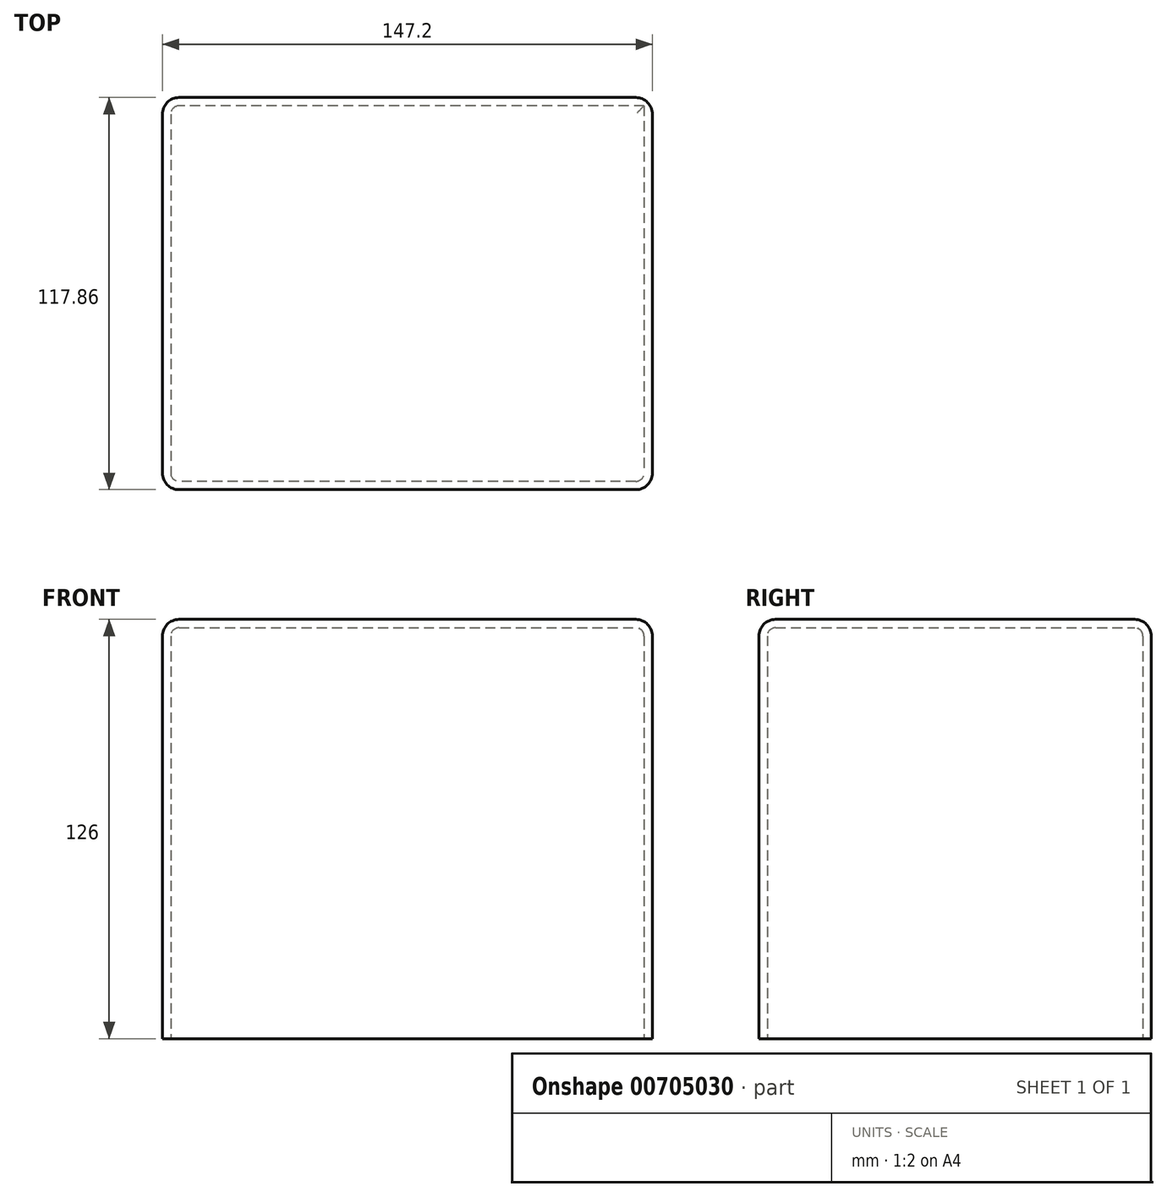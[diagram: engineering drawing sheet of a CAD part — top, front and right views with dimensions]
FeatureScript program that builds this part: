
annotation { "Feature Type Name" : "Feature", "Feature Type Description" : "" }
export const myFeature = defineFeature(function(context is Context, id is Id, definition is map)
    precondition{}
    {
        {
            var Q0;
            Q0=qCreatedBy(makeId("Top.planeOp"),FACE);
            var sketch = newSketch(context, id + "F0", { "sketchPlane" : qUnion([Q0])});
            skLineSegment(sketch, "E0.bottom", {"start": v(73.6, 58.93) * mm, "end": v(-73.6, 58.93) * mm});
            skLineSegment(sketch, "E0.top", {"start": v(73.6, -58.93) * mm, "end": v(-73.6, -58.93) * mm});
            skLineSegment(sketch, "E0.left", {"start": v(73.6, 58.93) * mm, "end": v(73.6, -58.93) * mm});
            skLineSegment(sketch, "E0.right", {"start": v(-73.6, 58.93) * mm, "end": v(-73.6, -58.93) * mm});
            skPoint(sketch, "E0.middle", {"position": v(0, 0) * mm});
            skSolve(sketch);
        }
        {
            var Q0;
            Q0=makeQuery(id+"F0.imprint","IMPRINT",FACE,{"disambiguationData":[TD([[makeQuery(id+"F0.imprint","IMPRINT",EDGE,{"derivedFrom":sQuery(id+"F0.wireOp",EDGE,"E0.bottom")}),1.0]])]});
            extrude(context, id + "F1", {"entities" : qUnion([Q0]), "depth" : 126 * mm, "offsetDistance" : 25 * mm});
        }
        {
            var Q0;
            Q0=makeQuery(id+"F1.opExtrude","SWEPT_EDGE",EDGE,{"disambiguationData":[OSD([sQuery(id+"F0.wireOp",EDGE,"E0.top"),sQuery(id+"F0.wireOp",EDGE,"E0.right")])]});
            var Q1;
            Q1=makeQuery(id+"F1.opExtrude","SWEPT_EDGE",EDGE,{"disambiguationData":[OSD([sQuery(id+"F0.wireOp",EDGE,"E0.top"),sQuery(id+"F0.wireOp",EDGE,"E0.left")])]});
            var Q2;
            Q2=makeQuery(id+"F1.opExtrude","CAP_EDGE",EDGE,{"disambiguationData":[OSD([sQuery(id+"F0.wireOp",EDGE,"E0.top")])],"isStart":false});
            var Q3;
            Q3=makeQuery(id+"F1.opExtrude","CAP_EDGE",EDGE,{"disambiguationData":[OSD([sQuery(id+"F0.wireOp",EDGE,"E0.right")])],"isStart":false});
            var Q4;
            Q4=makeQuery(id+"F1.opExtrude","CAP_EDGE",EDGE,{"disambiguationData":[OSD([sQuery(id+"F0.wireOp",EDGE,"E0.bottom")])],"isStart":false});
            var Q5;
            Q5=makeQuery(id+"F1.opExtrude","CAP_EDGE",EDGE,{"disambiguationData":[OSD([sQuery(id+"F0.wireOp",EDGE,"E0.left")])],"isStart":false});
            var Q6;
            Q6=makeQuery(id+"F1.opExtrude","SWEPT_EDGE",EDGE,{"disambiguationData":[OSD([sQuery(id+"F0.wireOp",EDGE,"E0.bottom"),sQuery(id+"F0.wireOp",EDGE,"E0.right")])]});
            fillet(context, id + "F2", {"entities" : qUnion([Q0, Q1, Q2, Q3, Q4, Q5, Q6]), "radius" : 5 * mm, "tangentPropagation" : true, "allowEdgeOverflow" : false});
        }
        {
            var Q0;
            Q0=makeQuery(id+"F1.opExtrude","CAP_FACE",FACE,{"disambiguationData":[OSD([sQuery(id+"F0.wireOp",EDGE,"E0.bottom"),sQuery(id+"F0.wireOp",EDGE,"E0.top"),sQuery(id+"F0.wireOp",EDGE,"E0.left"),sQuery(id+"F0.wireOp",EDGE,"E0.right")])],"isStart":true});
            shell(context, id + "F3", {"entities" : qUnion([Q0]), "thickness" : 2.5 * mm});
        }
        {
            var Q0;
            Q0=makeQuery(id+"F1.opExtrude","SWEPT_EDGE",EDGE,{"disambiguationData":[OSD([sQuery(id+"F0.wireOp",EDGE,"E0.bottom"),sQuery(id+"F0.wireOp",EDGE,"E0.left")])]});
            fillet(context, id + "F4", {"entities" : qUnion([Q0]), "radius" : 5 * mm, "tangentPropagation" : true, "allowEdgeOverflow" : false});
        }
    });
